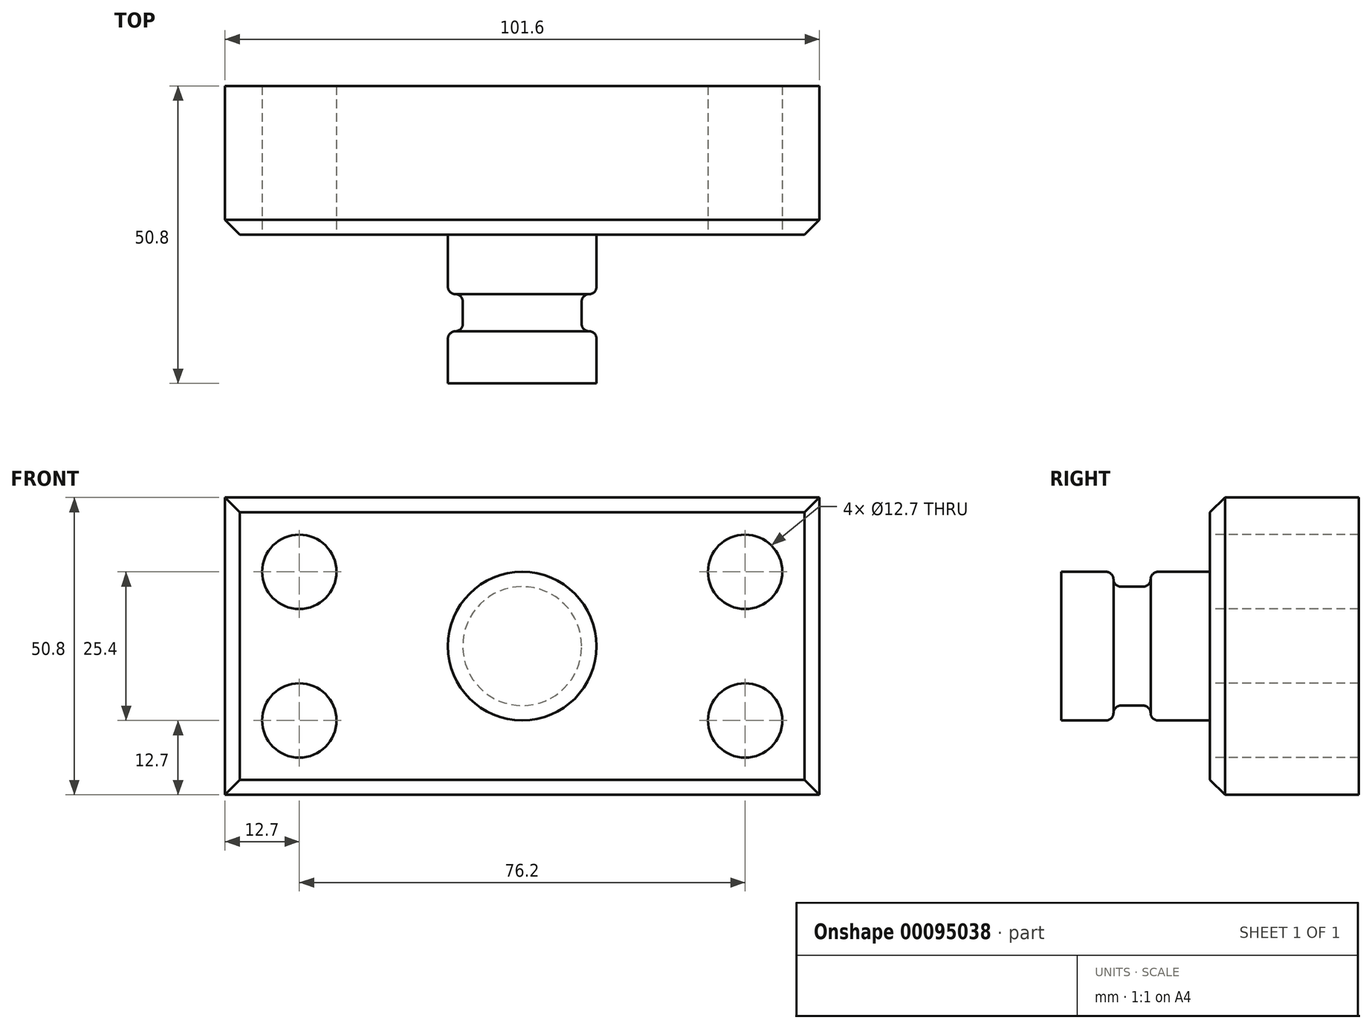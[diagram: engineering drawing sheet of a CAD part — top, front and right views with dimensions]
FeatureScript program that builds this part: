
annotation { "Feature Type Name" : "Feature", "Feature Type Description" : "" }
export const myFeature = defineFeature(function(context is Context, id is Id, definition is map)
    precondition{}
    {
        {
            var Q0;
            Q0=qCreatedBy(makeId("Front.planeOp"),FACE);
            var sketch = newSketch(context, id + "F0", { "sketchPlane" : qUnion([Q0])});
            skLineSegment(sketch, "E0.bottom", {"start": v(50.8, 25.4) * mm, "end": v(-50.8, 25.4) * mm});
            skLineSegment(sketch, "E0.top", {"start": v(50.8, -25.4) * mm, "end": v(-50.8, -25.4) * mm});
            skLineSegment(sketch, "E0.left", {"start": v(50.8, 25.4) * mm, "end": v(50.8, -25.4) * mm});
            skLineSegment(sketch, "E0.right", {"start": v(-50.8, 25.4) * mm, "end": v(-50.8, -25.4) * mm});
            skPoint(sketch, "E0.middle", {"position": v(0, 0) * mm});
            skSolve(sketch);
        }
        {
            var Q0;
            Q0 = qSketchRegion(id + "F0", true);
            extrude(context, id + "F1", {"entities" : qUnion([Q0]), "depth" : 25.4 * mm});
        }
        {
            var Q0;
            Q0=makeQuery(id+"F1.opExtrude","CAP_FACE",FACE,{"disambiguationData":[OSD([sQuery(id+"F0.wireOp",EDGE,"E0.bottom"),sQuery(id+"F0.wireOp",EDGE,"E0.top"),sQuery(id+"F0.wireOp",EDGE,"E0.left"),sQuery(id+"F0.wireOp",EDGE,"E0.right")])],"isStart":false});
            var sketch = newSketch(context, id + "F2", { "sketchPlane" : qUnion([Q0])});
            skCircle(sketch, "E1", {"center": v(-38.1, 12.7) * mm, "radius": 6.35 * mm});
            skCircle(sketch, "E2", {"center": v(-38.1, -12.7) * mm, "radius": 6.35 * mm});
            skCircle(sketch, "E3", {"center": v(38.1, -12.7) * mm, "radius": 6.35 * mm});
            skCircle(sketch, "E4", {"center": v(38.1, 12.7) * mm, "radius": 6.35 * mm});
            skSolve(sketch);
        }
        {
            var Q0;
            Q0 = qSketchRegion(id + "F2", true);
            extrude(context, id + "F3", {"entities" : qUnion([Q0]), "operationType" : NewBodyOperationType.REMOVE, "endBound" : BoundingType.THROUGH_ALL, "oppositeDirection" : true, "depth" : 25.4 * mm});
        }
        {
            var Q0;
            Q0=qCreatedBy(makeId("Top.planeOp"),FACE);
            var sketch = newSketch(context, id + "F4", { "sketchPlane" : qUnion([Q0])});
            skLineSegment(sketch, "E5.bottom", {"start": v(0, -25.4) * mm, "end": v(-12.7, -25.4) * mm});
            skLineSegment(sketch, "E5.top", {"start": v(0, -50.8) * mm, "end": v(-12.7, -50.8) * mm});
            skLineSegment(sketch, "E5.left", {"start": v(0, -25.4) * mm, "end": v(0, -50.8) * mm});
            skLineSegment(sketch, "E5.right", {"start": v(-12.7, -25.4) * mm, "end": v(-12.7, -50.8) * mm});
            skSolve(sketch);
        }
        {
            var Q0;
            Q0 = qSketchRegion(id + "F4", true);
            var Q1;
            Q1=sQuery(id+"F4.wireOp",EDGE,"E5.left");
            revolve(context, id + "F5", {"operationType" : NewBodyOperationType.ADD, "entities" : qUnion([Q0]), "axis" : qUnion([Q1]), "revolveType" : RevolveType.FULL});
        }
        {
            var Q0;
            Q0=qCreatedBy(makeId("Top.planeOp"),FACE);
            var sketch = newSketch(context, id + "F6", { "sketchPlane" : qUnion([Q0])});
            skLineSegment(sketch, "E6.bottom", {"start": v(-17.14, -41.9) * mm, "end": v(-10.16, -41.9) * mm});
            skLineSegment(sketch, "E6.top", {"start": v(-17.14, -35.56) * mm, "end": v(-10.16, -35.56) * mm});
            skLineSegment(sketch, "E6.left", {"start": v(-17.14, -41.91) * mm, "end": v(-17.14, -35.56) * mm});
            skLineSegment(sketch, "E6.right", {"start": v(-10.16, -41.9) * mm, "end": v(-10.16, -35.56) * mm});
            skLineSegment(sketch, "E7", {"start": v(0, 0) * mm, "end": v(0, -65.88) * mm, "construction": true});
            skSolve(sketch);
        }
        {
            var Q0;
            Q0=makeQuery(id+"F6.imprint","IMPRINT",FACE,{"disambiguationData":[TD([[makeQuery(id+"F6.imprint","IMPRINT",EDGE,{"derivedFrom":sQuery(id+"F6.wireOp",EDGE,"E6.bottom")}),1.0]])]});
            var Q1;
            Q1=sQuery(id+"F6.wireOp",EDGE,"E7");
            revolve(context, id + "F7", {"operationType" : NewBodyOperationType.REMOVE, "entities" : qUnion([Q0]), "axis" : qUnion([Q1]), "revolveType" : RevolveType.FULL, "oppositeDirection" : true});
        }
        {
            var Q0;
            Q0=makeQuery(id+"F5.opRevolve","SWEPT_EDGE",EDGE,{"disambiguationData":[OSD([sQuery(id+"F4.wireOp",EDGE,"E5.bottom"),sQuery(id+"F4.wireOp",EDGE,"E5.right")])]});
            var Q1;
            Q1=makeQuery(id+"F7.boolean.opBoolean","COPY",EDGE,{"derivedFrom":makeQuery(id+"F7.opRevolve","SWEPT_EDGE",EDGE,{"disambiguationData":[OSD([sQuery(id+"F6.wireOp",EDGE,"E6.bottom"),sQuery(id+"F6.wireOp",EDGE,"E6.right")])]})});
            var Q2;
            Q2=makeQuery(id+"F7.boolean.opBoolean","COPY",EDGE,{"derivedFrom":makeQuery(id+"F7.opRevolve","SWEPT_EDGE",EDGE,{"disambiguationData":[OSD([sQuery(id+"F6.wireOp",EDGE,"E6.top"),sQuery(id+"F6.wireOp",EDGE,"E6.right")])]})});
            var Q3;
            Q3=makeQuery(id+"F7.boolean.opBoolean","INTERSECT",EDGE,{"derivedFrom":[makeQuery(id+"F5.opRevolve","SWEPT_FACE",FACE,{"disambiguationData":[OSD([sQuery(id+"F4.wireOp",EDGE,"E5.right")])]}),makeQuery(id+"F7.opRevolve","SWEPT_FACE",FACE,{"disambiguationData":[OSD([sQuery(id+"F6.wireOp",EDGE,"E6.bottom")])]})]});
            var Q4;
            Q4=makeQuery(id+"F7.boolean.opBoolean","INTERSECT",EDGE,{"derivedFrom":[makeQuery(id+"F5.opRevolve","SWEPT_FACE",FACE,{"disambiguationData":[OSD([sQuery(id+"F4.wireOp",EDGE,"E5.right")])]}),makeQuery(id+"F7.opRevolve","SWEPT_FACE",FACE,{"disambiguationData":[OSD([sQuery(id+"F6.wireOp",EDGE,"E6.top")])]})]});
            fillet(context, id + "F8", {"entities" : qUnion([Q0, Q1, Q2, Q3, Q4]), "radius" : 1.27 * mm, "tangentPropagation" : true, "allowEdgeOverflow" : false});
        }
        {
            var Q0;
            Q0=makeQuery(id+"F1.opExtrude","CAP_EDGE",EDGE,{"disambiguationData":[OSD([sQuery(id+"F0.wireOp",EDGE,"E0.top")])],"isStart":false});
            var Q1;
            Q1=makeQuery(id+"F1.opExtrude","CAP_EDGE",EDGE,{"disambiguationData":[OSD([sQuery(id+"F0.wireOp",EDGE,"E0.right")])],"isStart":false});
            var Q2;
            Q2=makeQuery(id+"F1.opExtrude","CAP_EDGE",EDGE,{"disambiguationData":[OSD([sQuery(id+"F0.wireOp",EDGE,"E0.bottom")])],"isStart":false});
            var Q3;
            Q3=makeQuery(id+"F1.opExtrude","CAP_EDGE",EDGE,{"disambiguationData":[OSD([sQuery(id+"F0.wireOp",EDGE,"E0.left")])],"isStart":false});
            chamfer(context, id + "F9", {"entities" : qUnion([Q0, Q1, Q2, Q3]), "width" : 2.54 * mm, "tangentPropagation" : true});
        }
    });
